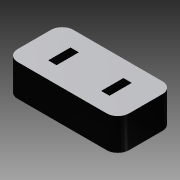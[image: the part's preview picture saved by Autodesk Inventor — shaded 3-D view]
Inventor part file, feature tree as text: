
AUTODESK INVENTOR PART (.ipt)
format: ipt  version: 2013 (Build 170138000, 138)  size: 97,792 bytes
history: native  units: mm
features: extrude x1, fillet x1, sketch x1
ambient origin geometry x8: Origin, YZ Plane, XZ Plane, XY Plane, X Axis, Y Axis, Z Axis, Center Point
bodies: Solid1 (feature_tree)
feature tree (3):
  extrude  "Extrusion1"  Depth=10.0mm
  fillet  "Fillet1"  Radius=8.0mm
  sketch  "Sketch1"  dims[d0=20.0mm d2=10.0mm d3=8.0mm d4=1.5mm d5=4.0mm d6=5.715mm d7=0.0mm d8=2.0mm]
